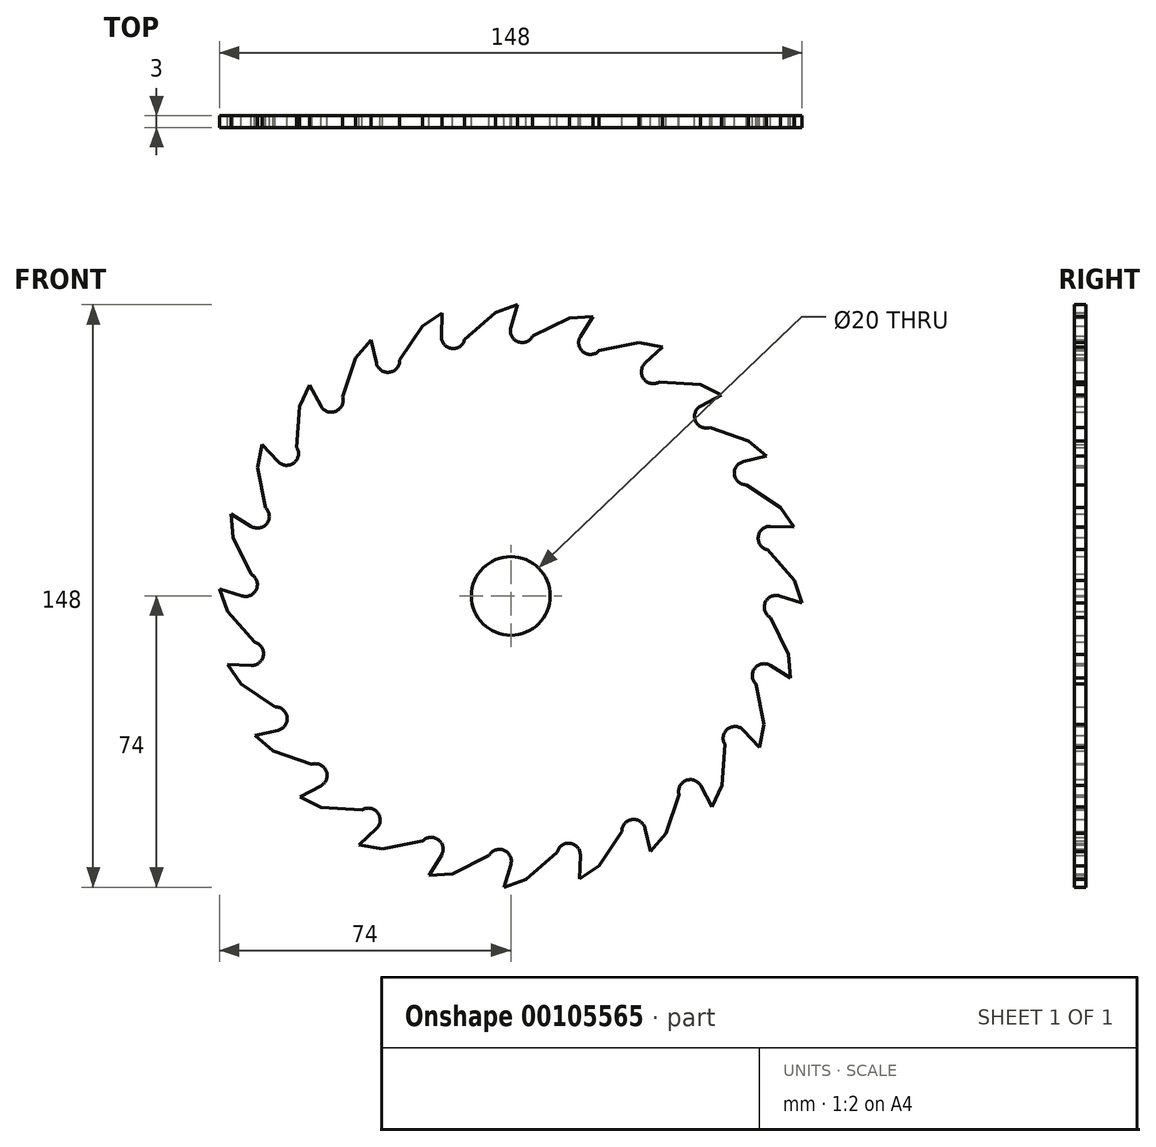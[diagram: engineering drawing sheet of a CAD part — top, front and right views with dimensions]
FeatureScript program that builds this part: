
annotation { "Feature Type Name" : "Feature", "Feature Type Description" : "" }
export const myFeature = defineFeature(function(context is Context, id is Id, definition is map)
    precondition{}
    {
        {
            var Q0;
            Q0=qCreatedBy(makeId("Front.planeOp"),FACE);
            var sketch = newSketch(context, id + "F0", { "sketchPlane" : qUnion([Q0])});
            skLineSegment(sketch, "E0", {"start": v(-11.75, 65.15) * mm, "end": v(-3.92, 72) * mm});
            skLineSegment(sketch, "E1", {"start": v(-3.92, 72) * mm, "end": v(1.74, 74) * mm});
            skLineSegment(sketch, "E2", {"start": v(1.74, 74) * mm, "end": v(0, 68.26) * mm});
            skArc(sketch, "E3", {"start": v(0, 68.26) * mm, "mid": v(1.72, 64.62) * mm, "end": v(5.52, 65.97) * mm});
            skLineSegment(sketch, "E4.1.0", {"start": v(-28.2, 59.89) * mm, "end": v(-22.42, 68.54) * mm});
            skLineSegment(sketch, "E4.1.1", {"start": v(-22.42, 68.54) * mm, "end": v(-17.47, 71.93) * mm});
            skLineSegment(sketch, "E4.1.2", {"start": v(-17.47, 71.93) * mm, "end": v(-17.67, 65.93) * mm});
            skArc(sketch, "E4.1.3", {"start": v(-17.67, 65.93) * mm, "mid": v(-15.06, 62.86) * mm, "end": v(-11.75, 65.15) * mm});
            skLineSegment(sketch, "E4.2.0", {"start": v(-42.75, 50.55) * mm, "end": v(-39.4, 60.4) * mm});
            skLineSegment(sketch, "E4.2.1", {"start": v(-39.4, 60.4) * mm, "end": v(-35.5, 64.96) * mm});
            skLineSegment(sketch, "E4.2.2", {"start": v(-35.5, 64.96) * mm, "end": v(-34.13, 59.11) * mm});
            skArc(sketch, "E4.2.3", {"start": v(-34.13, 59.11) * mm, "mid": v(-30.82, 56.82) * mm, "end": v(-28.2, 59.89) * mm});
            skLineSegment(sketch, "E4.3.0", {"start": v(-54.37, 37.76) * mm, "end": v(-53.68, 48.15) * mm});
            skLineSegment(sketch, "E4.3.1", {"start": v(-53.68, 48.15) * mm, "end": v(-51.1, 53.56) * mm});
            skLineSegment(sketch, "E4.3.2", {"start": v(-51.1, 53.56) * mm, "end": v(-48.27, 48.27) * mm});
            skArc(sketch, "E4.3.3", {"start": v(-48.27, 48.27) * mm, "mid": v(-44.47, 46.9) * mm, "end": v(-42.75, 50.55) * mm});
            skLineSegment(sketch, "E4.4.0", {"start": v(-62.3, 22.4) * mm, "end": v(-64.32, 32.61) * mm});
            skLineSegment(sketch, "E4.4.1", {"start": v(-64.32, 32.61) * mm, "end": v(-63.21, 38.5) * mm});
            skLineSegment(sketch, "E4.4.2", {"start": v(-63.21, 38.5) * mm, "end": v(-59.11, 34.13) * mm});
            skArc(sketch, "E4.4.3", {"start": v(-59.11, 34.13) * mm, "mid": v(-55.1, 33.8) * mm, "end": v(-54.37, 37.76) * mm});
            skLineSegment(sketch, "E4.5.0", {"start": v(-65.97, 5.52) * mm, "end": v(-70.56, 14.85) * mm});
            skLineSegment(sketch, "E4.5.1", {"start": v(-70.56, 14.85) * mm, "end": v(-71.03, 20.84) * mm});
            skLineSegment(sketch, "E4.5.2", {"start": v(-71.03, 20.84) * mm, "end": v(-65.93, 17.67) * mm});
            skArc(sketch, "E4.5.3", {"start": v(-65.93, 17.67) * mm, "mid": v(-61.97, 18.39) * mm, "end": v(-62.3, 22.4) * mm});
            skLineSegment(sketch, "E4.6.0", {"start": v(-65.15, -11.75) * mm, "end": v(-72, -3.92) * mm});
            skLineSegment(sketch, "E4.6.1", {"start": v(-72, -3.92) * mm, "end": v(-74, 1.74) * mm});
            skLineSegment(sketch, "E4.6.2", {"start": v(-74, 1.74) * mm, "end": v(-68.26, 0) * mm});
            skArc(sketch, "E4.6.3", {"start": v(-68.26, 0) * mm, "mid": v(-64.62, 1.72) * mm, "end": v(-65.97, 5.52) * mm});
            skLineSegment(sketch, "E4.7.0", {"start": v(-59.89, -28.2) * mm, "end": v(-68.54, -22.42) * mm});
            skLineSegment(sketch, "E4.7.1", {"start": v(-68.54, -22.42) * mm, "end": v(-71.93, -17.47) * mm});
            skLineSegment(sketch, "E4.7.2", {"start": v(-71.93, -17.47) * mm, "end": v(-65.93, -17.67) * mm});
            skArc(sketch, "E4.7.3", {"start": v(-65.93, -17.67) * mm, "mid": v(-62.86, -15.06) * mm, "end": v(-65.15, -11.75) * mm});
            skPoint(sketch, "E4.center", {"position": v(0, 0) * mm});
            skLineSegment(sketch, "E5.1.8.0", {"start": v(-50.55, -42.75) * mm, "end": v(-60.4, -39.4) * mm});
            skLineSegment(sketch, "E5.3.8.0", {"start": v(-60.4, -39.4) * mm, "end": v(-64.96, -35.5) * mm});
            skLineSegment(sketch, "E5.6.8.0", {"start": v(-64.96, -35.5) * mm, "end": v(-59.11, -34.13) * mm});
            skArc(sketch, "E5.9.8.0", {"start": v(-59.11, -34.13) * mm, "mid": v(-56.82, -30.82) * mm, "end": v(-59.89, -28.2) * mm});
            skLineSegment(sketch, "E6.1.9.0", {"start": v(-37.76, -54.37) * mm, "end": v(-48.15, -53.68) * mm});
            skLineSegment(sketch, "E6.3.9.0", {"start": v(-48.15, -53.68) * mm, "end": v(-53.56, -51.1) * mm});
            skLineSegment(sketch, "E6.6.9.0", {"start": v(-53.56, -51.1) * mm, "end": v(-48.27, -48.27) * mm});
            skArc(sketch, "E6.9.9.0", {"start": v(-48.27, -48.27) * mm, "mid": v(-46.9, -44.47) * mm, "end": v(-50.55, -42.75) * mm});
            skLineSegment(sketch, "E7.1.10.0", {"start": v(-22.4, -62.3) * mm, "end": v(-32.61, -64.32) * mm});
            skLineSegment(sketch, "E7.3.10.0", {"start": v(-32.61, -64.32) * mm, "end": v(-38.5, -63.21) * mm});
            skLineSegment(sketch, "E7.6.10.0", {"start": v(-38.5, -63.21) * mm, "end": v(-34.13, -59.11) * mm});
            skArc(sketch, "E7.9.10.0", {"start": v(-34.13, -59.11) * mm, "mid": v(-33.8, -55.1) * mm, "end": v(-37.76, -54.37) * mm});
            skLineSegment(sketch, "E8.1.11.0", {"start": v(-5.52, -65.97) * mm, "end": v(-14.85, -70.56) * mm});
            skLineSegment(sketch, "E8.3.11.0", {"start": v(-14.85, -70.56) * mm, "end": v(-20.84, -71.03) * mm});
            skLineSegment(sketch, "E8.6.11.0", {"start": v(-20.84, -71.03) * mm, "end": v(-17.67, -65.93) * mm});
            skArc(sketch, "E8.9.11.0", {"start": v(-17.67, -65.93) * mm, "mid": v(-18.39, -61.97) * mm, "end": v(-22.4, -62.3) * mm});
            skLineSegment(sketch, "E9.1.12.0", {"start": v(11.75, -65.15) * mm, "end": v(3.92, -72) * mm});
            skLineSegment(sketch, "E9.3.12.0", {"start": v(3.92, -72) * mm, "end": v(-1.74, -74) * mm});
            skLineSegment(sketch, "E9.6.12.0", {"start": v(-1.74, -74) * mm, "end": v(0, -68.26) * mm});
            skArc(sketch, "E9.9.12.0", {"start": v(0, -68.26) * mm, "mid": v(-1.72, -64.62) * mm, "end": v(-5.52, -65.97) * mm});
            skLineSegment(sketch, "E10.1.13.0", {"start": v(28.2, -59.89) * mm, "end": v(22.42, -68.54) * mm});
            skLineSegment(sketch, "E10.3.13.0", {"start": v(22.42, -68.54) * mm, "end": v(17.47, -71.93) * mm});
            skLineSegment(sketch, "E10.6.13.0", {"start": v(17.47, -71.93) * mm, "end": v(17.67, -65.93) * mm});
            skArc(sketch, "E10.9.13.0", {"start": v(17.67, -65.93) * mm, "mid": v(15.06, -62.86) * mm, "end": v(11.75, -65.15) * mm});
            skLineSegment(sketch, "E11.1.14.0", {"start": v(42.75, -50.55) * mm, "end": v(39.4, -60.4) * mm});
            skLineSegment(sketch, "E11.3.14.0", {"start": v(39.4, -60.4) * mm, "end": v(35.5, -64.96) * mm});
            skLineSegment(sketch, "E11.6.14.0", {"start": v(35.5, -64.96) * mm, "end": v(34.13, -59.11) * mm});
            skArc(sketch, "E11.9.14.0", {"start": v(34.13, -59.11) * mm, "mid": v(30.82, -56.82) * mm, "end": v(28.2, -59.89) * mm});
            skLineSegment(sketch, "E12.1.15.0", {"start": v(54.37, -37.76) * mm, "end": v(53.68, -48.15) * mm});
            skLineSegment(sketch, "E12.3.15.0", {"start": v(53.68, -48.15) * mm, "end": v(51.1, -53.56) * mm});
            skLineSegment(sketch, "E12.6.15.0", {"start": v(51.1, -53.56) * mm, "end": v(48.27, -48.27) * mm});
            skArc(sketch, "E12.9.15.0", {"start": v(48.27, -48.27) * mm, "mid": v(44.47, -46.9) * mm, "end": v(42.75, -50.55) * mm});
            skLineSegment(sketch, "E13.1.16.0", {"start": v(62.3, -22.4) * mm, "end": v(64.32, -32.61) * mm});
            skLineSegment(sketch, "E13.3.16.0", {"start": v(64.32, -32.61) * mm, "end": v(63.21, -38.5) * mm});
            skLineSegment(sketch, "E13.6.16.0", {"start": v(63.21, -38.5) * mm, "end": v(59.11, -34.13) * mm});
            skArc(sketch, "E13.9.16.0", {"start": v(59.11, -34.13) * mm, "mid": v(55.1, -33.8) * mm, "end": v(54.37, -37.76) * mm});
            skLineSegment(sketch, "E14.1.17.0", {"start": v(65.97, -5.52) * mm, "end": v(70.56, -14.85) * mm});
            skLineSegment(sketch, "E14.3.17.0", {"start": v(70.56, -14.85) * mm, "end": v(71.03, -20.84) * mm});
            skLineSegment(sketch, "E14.6.17.0", {"start": v(71.03, -20.84) * mm, "end": v(65.93, -17.67) * mm});
            skArc(sketch, "E14.9.17.0", {"start": v(65.93, -17.67) * mm, "mid": v(61.97, -18.39) * mm, "end": v(62.3, -22.4) * mm});
            skLineSegment(sketch, "E15.1.18.0", {"start": v(65.15, 11.75) * mm, "end": v(72, 3.92) * mm});
            skLineSegment(sketch, "E15.3.18.0", {"start": v(72, 3.92) * mm, "end": v(74, -1.74) * mm});
            skLineSegment(sketch, "E15.6.18.0", {"start": v(74, -1.74) * mm, "end": v(68.26, 0) * mm});
            skArc(sketch, "E15.9.18.0", {"start": v(68.26, 0) * mm, "mid": v(64.62, -1.72) * mm, "end": v(65.97, -5.52) * mm});
            skLineSegment(sketch, "E16.1.19.0", {"start": v(59.89, 28.2) * mm, "end": v(68.54, 22.42) * mm});
            skLineSegment(sketch, "E16.3.19.0", {"start": v(68.54, 22.42) * mm, "end": v(71.93, 17.47) * mm});
            skLineSegment(sketch, "E16.6.19.0", {"start": v(71.93, 17.47) * mm, "end": v(65.93, 17.67) * mm});
            skArc(sketch, "E16.9.19.0", {"start": v(65.93, 17.67) * mm, "mid": v(62.86, 15.06) * mm, "end": v(65.15, 11.75) * mm});
            skLineSegment(sketch, "E17.1.20.0", {"start": v(50.55, 42.75) * mm, "end": v(60.4, 39.4) * mm});
            skLineSegment(sketch, "E17.3.20.0", {"start": v(60.4, 39.4) * mm, "end": v(64.96, 35.5) * mm});
            skLineSegment(sketch, "E17.6.20.0", {"start": v(64.96, 35.5) * mm, "end": v(59.11, 34.13) * mm});
            skArc(sketch, "E17.9.20.0", {"start": v(59.11, 34.13) * mm, "mid": v(56.82, 30.82) * mm, "end": v(59.89, 28.2) * mm});
            skLineSegment(sketch, "E18.1.21.0", {"start": v(37.76, 54.37) * mm, "end": v(48.15, 53.68) * mm});
            skLineSegment(sketch, "E18.3.21.0", {"start": v(48.15, 53.68) * mm, "end": v(53.56, 51.1) * mm});
            skLineSegment(sketch, "E18.6.21.0", {"start": v(53.56, 51.1) * mm, "end": v(48.27, 48.27) * mm});
            skArc(sketch, "E18.9.21.0", {"start": v(48.27, 48.27) * mm, "mid": v(46.9, 44.47) * mm, "end": v(50.55, 42.75) * mm});
            skLineSegment(sketch, "E19.1.22.0", {"start": v(22.4, 62.3) * mm, "end": v(32.61, 64.32) * mm});
            skLineSegment(sketch, "E19.3.22.0", {"start": v(32.61, 64.32) * mm, "end": v(38.5, 63.21) * mm});
            skLineSegment(sketch, "E19.6.22.0", {"start": v(38.5, 63.21) * mm, "end": v(34.13, 59.11) * mm});
            skArc(sketch, "E19.9.22.0", {"start": v(34.13, 59.11) * mm, "mid": v(33.8, 55.1) * mm, "end": v(37.76, 54.37) * mm});
            skLineSegment(sketch, "E20.1.23.0", {"start": v(5.52, 65.97) * mm, "end": v(14.85, 70.56) * mm});
            skLineSegment(sketch, "E20.3.23.0", {"start": v(14.85, 70.56) * mm, "end": v(20.84, 71.03) * mm});
            skLineSegment(sketch, "E20.6.23.0", {"start": v(20.84, 71.03) * mm, "end": v(17.67, 65.93) * mm});
            skArc(sketch, "E20.9.23.0", {"start": v(17.67, 65.93) * mm, "mid": v(18.39, 61.97) * mm, "end": v(22.4, 62.3) * mm});
            skCircle(sketch, "E21", {"center": v(0, 0) * mm, "radius": 10 * mm});
            skSolve(sketch);
        }
        {
            var Q0;
            {var subQ17=sQuery(id+"F0.wireOp",EDGE,"E0");Q0=makeQuery(id+"F0.imprint","IMPRINT",FACE,{"disambiguationData":[TD([[makeQuery(id+"F0.imprint","IMPRINT",EDGE,{"derivedFrom":subQ17}),-1.0]])]});}
            extrude(context, id + "F1", {"entities" : qUnion([Q0]), "depth" : 3 * mm});
        }
    });
